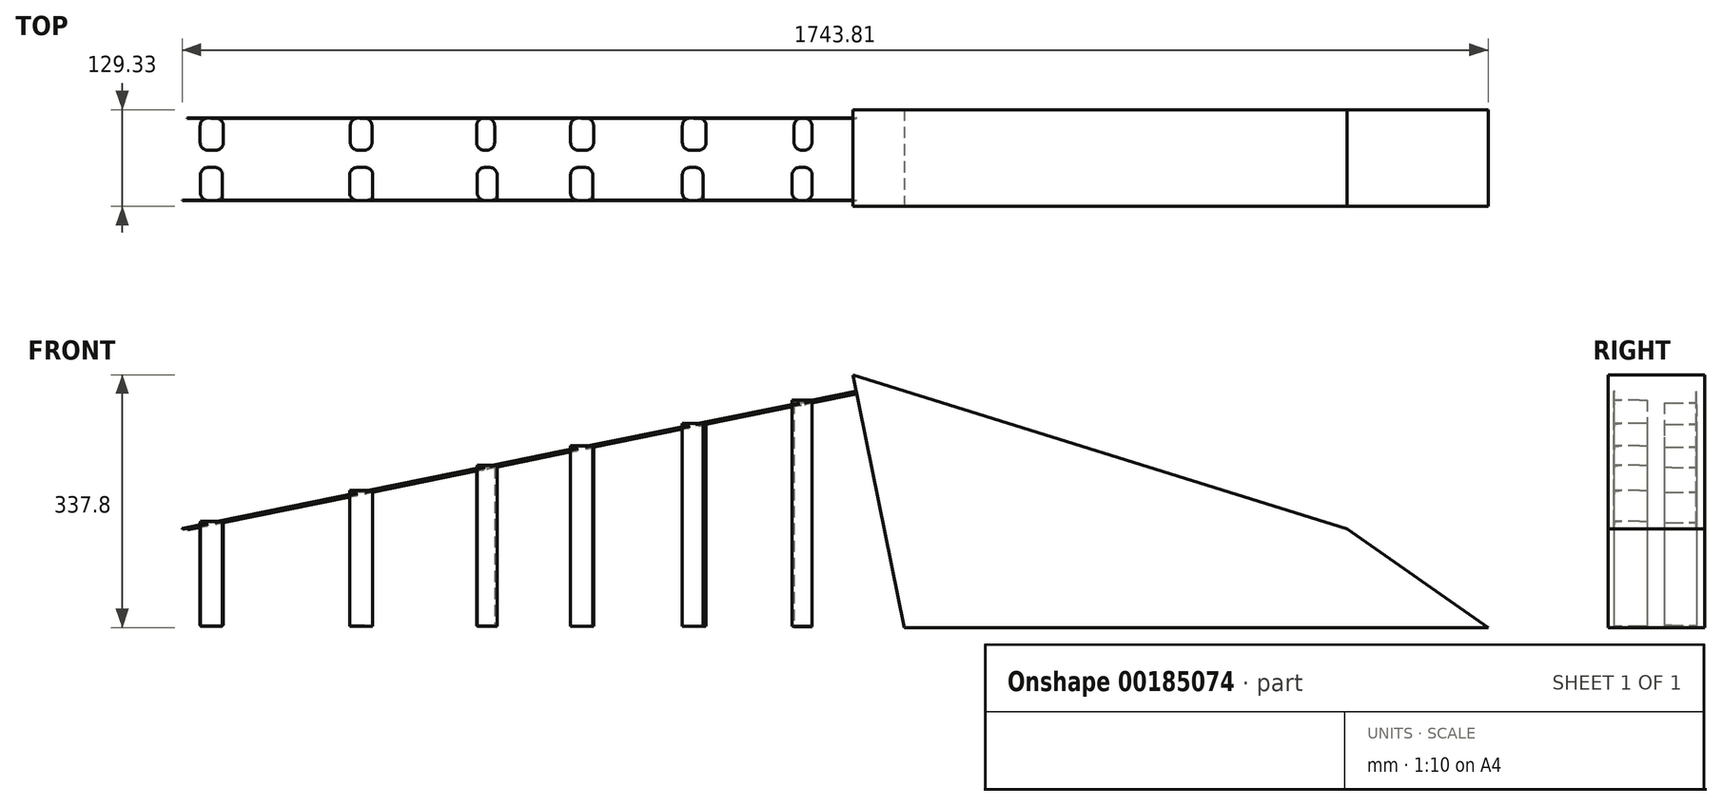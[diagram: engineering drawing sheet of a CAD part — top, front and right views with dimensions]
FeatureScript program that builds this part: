
annotation { "Feature Type Name" : "Feature", "Feature Type Description" : "" }
export const myFeature = defineFeature(function(context is Context, id is Id, definition is map)
    precondition{}
    {
        {
            var Q0;
            Q0=qCreatedBy(makeId("Front.planeOp"),FACE);
            var sketch = newSketch(context, id + "F0", { "sketchPlane" : qUnion([Q0])});
            skLineSegment(sketch, "E0", {"start": v(883.17, -182.99) * mm, "end": v(694.63, -51.4) * mm});
            skLineSegment(sketch, "E1", {"start": v(694.63, -51.4) * mm, "end": v(34.75, 154.8) * mm});
            skLineSegment(sketch, "E2", {"start": v(34.75, 154.8) * mm, "end": v(103.5, -182.99) * mm});
            skLineSegment(sketch, "E3", {"start": v(103.5, -182.99) * mm, "end": v(883.17, -182.99) * mm});
            skSolve(sketch);
        }
        {
            var Q0;
            Q0 = qSketchRegion(id + "F0", true);
            extrude(context, id + "F1", {"entities" : qUnion([Q0]), "oppositeDirection" : true, "depth" : 129.33 * mm});
        }
        {
            var Q0;
            Q0=makeQuery(id+"F1.opExtrude","SWEPT_FACE",FACE,{"disambiguationData":[OSD([sQuery(id+"F0.wireOp",EDGE,"E2")])]});
            var sketch = newSketch(context, id + "F2", { "sketchPlane" : qUnion([Q0])});
            skCircle(sketch, "E4", {"center": v(-33.96, 115.05) * mm, "radius": 26.4 * mm});
            skCircle(sketch, "E5", {"center": v(-91.6, 115.05) * mm, "radius": 26.3 * mm});
            skSolve(sketch);
        }
        {
            var Q0;
            Q0=sQuery(id+"F2.wireOp",EDGE,"E4");
            var Q1;
            Q1=sQuery(id+"F2.wireOp",EDGE,"E5");
            extrude(context, id + "F3", {"bodyType" : ToolBodyType.SURFACE, "surfaceEntities" : qUnion([Q0, Q1]), "depth" : 912.42 * mm});
        }
        {
            var Q0;
            Q0=makeQuery(id+"F1.opExtrude","SWEPT_FACE",FACE,{"disambiguationData":[OSD([sQuery(id+"F0.wireOp",EDGE,"E2")])]});
            var sketch = newSketch(context, id + "F4", { "sketchPlane" : qUnion([Q0])});
            skLineSegment(sketch, "E6.bottom", {"start": v(-8.52, 122.16) * mm, "end": v(-7.92, 122.16) * mm});
            skLineSegment(sketch, "E6.top", {"start": v(-8.52, 120.85) * mm, "end": v(-7.92, 120.85) * mm});
            skLineSegment(sketch, "E6.left", {"start": v(-8.52, 122.16) * mm, "end": v(-8.52, 120.85) * mm});
            skLineSegment(sketch, "E6.right", {"start": v(-7.92, 122.16) * mm, "end": v(-7.92, 120.85) * mm});
            skSolve(sketch);
        }
        {
            var Q0;
            Q0 = qSketchRegion(id + "F4", true);
            extrude(context, id + "F5", {"entities" : qUnion([Q0]), "operationType" : NewBodyOperationType.ADD, "depth" : 918.35 * mm});
        }
        {
            var Q0;
            Q0=makeQuery(id+"F5.opExtrude","SWEPT_FACE",FACE,{"disambiguationData":[OSD([sQuery(id+"F4.wireOp",EDGE,"E6.right")])]});
            var sketch = newSketch(context, id + "F6", { "sketchPlane" : qUnion([Q0])});
            skLineSegment(sketch, "E7.bottom", {"start": v(-19.45, 120.7) * mm, "end": v(-46.2, 120.7) * mm});
            skLineSegment(sketch, "E7.top", {"start": v(-19.45, -181.37) * mm, "end": v(-46.2, -181.37) * mm});
            skLineSegment(sketch, "E7.left", {"start": v(-19.45, 120.7) * mm, "end": v(-19.45, -181.37) * mm});
            skLineSegment(sketch, "E7.right", {"start": v(-46.2, 120.7) * mm, "end": v(-46.2, -181.37) * mm});
            skLineSegment(sketch, "E8.bottom", {"start": v(-165.16, 89.72) * mm, "end": v(-192.75, 89.72) * mm});
            skLineSegment(sketch, "E8.top", {"start": v(-165.16, -181.37) * mm, "end": v(-192.75, -181.37) * mm});
            skLineSegment(sketch, "E8.left", {"start": v(-165.16, 89.72) * mm, "end": v(-165.16, -181.37) * mm});
            skLineSegment(sketch, "E8.right", {"start": v(-192.75, 89.72) * mm, "end": v(-192.75, -181.37) * mm});
            skLineSegment(sketch, "E9.bottom", {"start": v(-312.41, 59.76) * mm, "end": v(-342.06, 59.76) * mm});
            skLineSegment(sketch, "E9.top", {"start": v(-312.41, -181.37) * mm, "end": v(-342.06, -181.37) * mm});
            skLineSegment(sketch, "E9.left", {"start": v(-312.41, 59.76) * mm, "end": v(-312.41, -181.37) * mm});
            skLineSegment(sketch, "E9.right", {"start": v(-342.06, 59.76) * mm, "end": v(-342.06, -181.37) * mm});
            skLineSegment(sketch, "E10.bottom", {"start": v(-440.02, 33.79) * mm, "end": v(-466.59, 33.79) * mm});
            skLineSegment(sketch, "E10.top", {"start": v(-440.02, -181.37) * mm, "end": v(-466.59, -181.37) * mm});
            skLineSegment(sketch, "E10.left", {"start": v(-440.02, 33.79) * mm, "end": v(-440.02, -181.37) * mm});
            skLineSegment(sketch, "E10.right", {"start": v(-466.59, 33.79) * mm, "end": v(-466.59, -181.37) * mm});
            skLineSegment(sketch, "E11.bottom", {"start": v(-606.07, 0) * mm, "end": v(-636.97, 0) * mm});
            skLineSegment(sketch, "E11.top", {"start": v(-606.07, -181.37) * mm, "end": v(-636.97, -181.37) * mm});
            skLineSegment(sketch, "E11.left", {"start": v(-606.07, 0) * mm, "end": v(-606.07, -181.37) * mm});
            skLineSegment(sketch, "E11.right", {"start": v(-636.97, 0) * mm, "end": v(-636.97, -181.37) * mm});
            skLineSegment(sketch, "E12.bottom", {"start": v(-806.8, -40.85) * mm, "end": v(-836.22, -40.85) * mm});
            skLineSegment(sketch, "E12.top", {"start": v(-806.8, -181.37) * mm, "end": v(-836.22, -181.37) * mm});
            skLineSegment(sketch, "E12.left", {"start": v(-806.8, -40.85) * mm, "end": v(-806.8, -181.37) * mm});
            skLineSegment(sketch, "E12.right", {"start": v(-836.22, -40.85) * mm, "end": v(-836.22, -181.37) * mm});
            skSolve(sketch);
        }
        {
            var Q0;
            Q0 = qSketchRegion(id + "F6", true);
            extrude(context, id + "F7", {"entities" : qUnion([Q0]), "operationType" : NewBodyOperationType.ADD, "oppositeDirection" : true, "depth" : 44.1 * mm});
        }
        {
            var Q0;
            Q0=makeQuery(id+"F1.opExtrude","SWEPT_FACE",FACE,{"disambiguationData":[OSD([sQuery(id+"F0.wireOp",EDGE,"E2")])]});
            var sketch = newSketch(context, id + "F8", { "sketchPlane" : qUnion([Q0])});
            skLineSegment(sketch, "E13.bottom", {"start": v(-117.63, 118.72) * mm, "end": v(-118.1, 118.72) * mm});
            skLineSegment(sketch, "E13.top", {"start": v(-117.63, 122) * mm, "end": v(-118.1, 122) * mm});
            skLineSegment(sketch, "E13.left", {"start": v(-117.63, 118.72) * mm, "end": v(-117.63, 122) * mm});
            skLineSegment(sketch, "E13.right", {"start": v(-118.1, 118.72) * mm, "end": v(-118.1, 122) * mm});
            skSolve(sketch);
        }
        {
            var Q0;
            Q0 = qSketchRegion(id + "F8", true);
            extrude(context, id + "F9", {"entities" : qUnion([Q0]), "operationType" : NewBodyOperationType.ADD, "depth" : 911.62 * mm});
        }
        {
            var Q0;
            Q0=makeQuery(id+"F9.opExtrude","SWEPT_FACE",FACE,{"disambiguationData":[OSD([sQuery(id+"F8.wireOp",EDGE,"E13.right")])]});
            var sketch = newSketch(context, id + "F10", { "sketchPlane" : qUnion([Q0])});
            skLineSegment(sketch, "E14.bottom", {"start": v(19.8, 117.13) * mm, "end": v(43.53, 117.13) * mm});
            skLineSegment(sketch, "E14.top", {"start": v(19.8, -182.09) * mm, "end": v(43.53, -182.09) * mm});
            skLineSegment(sketch, "E14.left", {"start": v(19.8, 117.13) * mm, "end": v(19.8, -182.09) * mm});
            skLineSegment(sketch, "E14.right", {"start": v(43.53, 117.13) * mm, "end": v(43.53, -182.09) * mm});
            skLineSegment(sketch, "E15.bottom", {"start": v(161.03, 88.4) * mm, "end": v(192.7, 88.4) * mm});
            skLineSegment(sketch, "E15.top", {"start": v(161.03, -181.24) * mm, "end": v(192.7, -181.24) * mm});
            skLineSegment(sketch, "E15.left", {"start": v(161.03, 88.4) * mm, "end": v(161.03, -181.24) * mm});
            skLineSegment(sketch, "E15.right", {"start": v(192.7, 88.4) * mm, "end": v(192.7, -181.24) * mm});
            skLineSegment(sketch, "E16.bottom", {"start": v(311.32, 57.8) * mm, "end": v(341.87, 57.8) * mm});
            skLineSegment(sketch, "E16.top", {"start": v(311.32, -181.24) * mm, "end": v(341.87, -181.24) * mm});
            skLineSegment(sketch, "E16.left", {"start": v(311.32, 57.8) * mm, "end": v(311.32, -181.24) * mm});
            skLineSegment(sketch, "E16.right", {"start": v(341.87, 57.8) * mm, "end": v(341.87, -181.24) * mm});
            skLineSegment(sketch, "E17.bottom", {"start": v(443.47, 30.92) * mm, "end": v(467.45, 30.92) * mm});
            skLineSegment(sketch, "E17.top", {"start": v(443.47, -180.4) * mm, "end": v(467.45, -180.4) * mm});
            skLineSegment(sketch, "E17.left", {"start": v(443.47, 30.92) * mm, "end": v(443.47, -180.4) * mm});
            skLineSegment(sketch, "E17.right", {"start": v(467.45, 30.92) * mm, "end": v(467.45, -180.4) * mm});
            skLineSegment(sketch, "E18.bottom", {"start": v(607.24, -2.4) * mm, "end": v(636, -2.4) * mm});
            skLineSegment(sketch, "E18.top", {"start": v(607.24, -180.4) * mm, "end": v(636, -180.4) * mm});
            skLineSegment(sketch, "E18.left", {"start": v(607.24, -2.4) * mm, "end": v(607.24, -180.4) * mm});
            skLineSegment(sketch, "E18.right", {"start": v(636, -2.4) * mm, "end": v(636, -180.4) * mm});
            skLineSegment(sketch, "E19.bottom", {"start": v(805.62, -42.78) * mm, "end": v(836.58, -42.78) * mm});
            skLineSegment(sketch, "E19.top", {"start": v(805.62, -180.4) * mm, "end": v(836.58, -180.4) * mm});
            skLineSegment(sketch, "E19.left", {"start": v(805.62, -42.78) * mm, "end": v(805.62, -180.4) * mm});
            skLineSegment(sketch, "E19.right", {"start": v(836.58, -42.78) * mm, "end": v(836.58, -180.4) * mm});
            skSolve(sketch);
        }
        {
            var Q0;
            Q0 = qSketchRegion(id + "F10", true);
            extrude(context, id + "F11", {"entities" : qUnion([Q0]), "operationType" : NewBodyOperationType.ADD, "oppositeDirection" : true, "depth" : 43.03 * mm});
        }
        {
            var Q0;
            Q0=makeQuery(id+"F11.opExtrude","CAP_EDGE",EDGE,{"disambiguationData":[OSD([sQuery(id+"F10.wireOp",EDGE,"E16.left")])],"isStart":false});
            var Q1;
            Q1=makeQuery(id+"F11.opExtrude","CAP_EDGE",EDGE,{"disambiguationData":[OSD([sQuery(id+"F10.wireOp",EDGE,"E18.left")])],"isStart":false});
            var Q2;
            Q2=makeQuery(id+"F7.opExtrude","CAP_EDGE",EDGE,{"disambiguationData":[OSD([sQuery(id+"F6.wireOp",EDGE,"E8.left")])],"isStart":true});
            var Q3;
            Q3=makeQuery(id+"F7.opExtrude","CAP_EDGE",EDGE,{"disambiguationData":[OSD([sQuery(id+"F6.wireOp",EDGE,"E9.left")])],"isStart":false});
            var Q4;
            Q4=makeQuery(id+"F11.opExtrude","CAP_EDGE",EDGE,{"disambiguationData":[OSD([sQuery(id+"F10.wireOp",EDGE,"E16.right")])],"isStart":false});
            var Q5;
            Q5=makeQuery(id+"F7.opExtrude","CAP_EDGE",EDGE,{"disambiguationData":[OSD([sQuery(id+"F6.wireOp",EDGE,"E11.right")])],"isStart":false});
            var Q6;
            Q6=makeQuery(id+"F11.opExtrude","CAP_EDGE",EDGE,{"disambiguationData":[OSD([sQuery(id+"F10.wireOp",EDGE,"E17.right")])],"isStart":false});
            var Q7;
            Q7=makeQuery(id+"F11.opExtrude","CAP_EDGE",EDGE,{"disambiguationData":[OSD([sQuery(id+"F10.wireOp",EDGE,"E19.left")])],"isStart":true});
            var Q8;
            Q8=makeQuery(id+"F7.opExtrude","CAP_EDGE",EDGE,{"disambiguationData":[OSD([sQuery(id+"F6.wireOp",EDGE,"E7.left")])],"isStart":false});
            var Q9;
            Q9=makeQuery(id+"F11.opExtrude","CAP_EDGE",EDGE,{"disambiguationData":[OSD([sQuery(id+"F10.wireOp",EDGE,"E19.left")])],"isStart":false});
            var Q10;
            Q10=makeQuery(id+"F11.opExtrude","CAP_EDGE",EDGE,{"disambiguationData":[OSD([sQuery(id+"F10.wireOp",EDGE,"E16.left")])],"isStart":true});
            var Q11;
            Q11=makeQuery(id+"F11.opExtrude","CAP_EDGE",EDGE,{"disambiguationData":[OSD([sQuery(id+"F10.wireOp",EDGE,"E14.right")])],"isStart":false});
            var Q12;
            Q12=makeQuery(id+"F7.opExtrude","CAP_EDGE",EDGE,{"disambiguationData":[OSD([sQuery(id+"F6.wireOp",EDGE,"E10.left")])],"isStart":true});
            var Q13;
            Q13=makeQuery(id+"F7.opExtrude","CAP_EDGE",EDGE,{"disambiguationData":[OSD([sQuery(id+"F6.wireOp",EDGE,"E11.left")])],"isStart":true});
            var Q14;
            Q14=makeQuery(id+"F11.opExtrude","CAP_EDGE",EDGE,{"disambiguationData":[OSD([sQuery(id+"F10.wireOp",EDGE,"E17.left")])],"isStart":true});
            var Q15;
            Q15=makeQuery(id+"F11.opExtrude","CAP_EDGE",EDGE,{"disambiguationData":[OSD([sQuery(id+"F10.wireOp",EDGE,"E14.left")])],"isStart":false});
            var Q16;
            {var subQ0=sQuery(id+"F6.wireOp",EDGE,"E11.right");Q16=makeQuery(id+"F7.boolean.opBoolean","SPLIT",EDGE,{"disambiguationData":[TD([makeQuery(id+"F5.opExtrude","SWEPT_FACE",FACE,{"disambiguationData":[OSD([sQuery(id+"F4.wireOp",EDGE,"E6.top")])]})])],"derivedFrom":makeQuery(id+"F7.opExtrude","CAP_EDGE",EDGE,{"disambiguationData":[OSD([subQ0])],"isStart":true})});}
            var Q17;
            Q17=makeQuery(id+"F11.opExtrude","CAP_EDGE",EDGE,{"disambiguationData":[OSD([sQuery(id+"F10.wireOp",EDGE,"E15.left")])],"isStart":false});
            var Q18;
            Q18=makeQuery(id+"F7.opExtrude","CAP_EDGE",EDGE,{"disambiguationData":[OSD([sQuery(id+"F6.wireOp",EDGE,"E12.right")])],"isStart":false});
            var Q19;
            {var subQ0=sQuery(id+"F10.wireOp",EDGE,"E19.right");Q19=makeQuery(id+"F11.boolean.opBoolean","SPLIT",EDGE,{"disambiguationData":[TD([makeQuery(id+"F9.opExtrude","SWEPT_FACE",FACE,{"disambiguationData":[OSD([sQuery(id+"F8.wireOp",EDGE,"E13.bottom")])]})])],"derivedFrom":makeQuery(id+"F11.opExtrude","CAP_EDGE",EDGE,{"disambiguationData":[OSD([subQ0])],"isStart":true})});}
            var Q20;
            {var subQ0=sQuery(id+"F6.wireOp",EDGE,"E8.right");Q20=makeQuery(id+"F7.boolean.opBoolean","SPLIT",EDGE,{"disambiguationData":[TD([makeQuery(id+"F5.opExtrude","SWEPT_FACE",FACE,{"disambiguationData":[OSD([sQuery(id+"F4.wireOp",EDGE,"E6.top")])]})])],"derivedFrom":makeQuery(id+"F7.opExtrude","CAP_EDGE",EDGE,{"disambiguationData":[OSD([subQ0])],"isStart":true})});}
            var Q21;
            Q21=makeQuery(id+"F7.opExtrude","CAP_EDGE",EDGE,{"disambiguationData":[OSD([sQuery(id+"F6.wireOp",EDGE,"E12.left")])],"isStart":false});
            var Q22;
            Q22=makeQuery(id+"F7.opExtrude","CAP_EDGE",EDGE,{"disambiguationData":[OSD([sQuery(id+"F6.wireOp",EDGE,"E12.left")])],"isStart":true});
            var Q23;
            {var subQ0=sQuery(id+"F10.wireOp",EDGE,"E18.right");Q23=makeQuery(id+"F11.boolean.opBoolean","SPLIT",EDGE,{"disambiguationData":[TD([makeQuery(id+"F9.opExtrude","SWEPT_FACE",FACE,{"disambiguationData":[OSD([sQuery(id+"F8.wireOp",EDGE,"E13.bottom")])]})])],"derivedFrom":makeQuery(id+"F11.opExtrude","CAP_EDGE",EDGE,{"disambiguationData":[OSD([subQ0])],"isStart":true})});}
            var Q24;
            Q24=makeQuery(id+"F7.opExtrude","CAP_EDGE",EDGE,{"disambiguationData":[OSD([sQuery(id+"F6.wireOp",EDGE,"E10.right")])],"isStart":false});
            var Q25;
            Q25=makeQuery(id+"F7.opExtrude","CAP_EDGE",EDGE,{"disambiguationData":[OSD([sQuery(id+"F6.wireOp",EDGE,"E9.left")])],"isStart":true});
            var Q26;
            Q26=makeQuery(id+"F7.opExtrude","CAP_EDGE",EDGE,{"disambiguationData":[OSD([sQuery(id+"F6.wireOp",EDGE,"E10.left")])],"isStart":false});
            var Q27;
            {var subQ0=sQuery(id+"F10.wireOp",EDGE,"E16.right");Q27=makeQuery(id+"F11.boolean.opBoolean","SPLIT",EDGE,{"disambiguationData":[TD([makeQuery(id+"F9.opExtrude","SWEPT_FACE",FACE,{"disambiguationData":[OSD([sQuery(id+"F8.wireOp",EDGE,"E13.bottom")])]})])],"derivedFrom":makeQuery(id+"F11.opExtrude","CAP_EDGE",EDGE,{"disambiguationData":[OSD([subQ0])],"isStart":true})});}
            var Q28;
            Q28=makeQuery(id+"F7.opExtrude","CAP_EDGE",EDGE,{"disambiguationData":[OSD([sQuery(id+"F6.wireOp",EDGE,"E9.right")])],"isStart":false});
            var Q29;
            {var subQ0=sQuery(id+"F10.wireOp",EDGE,"E17.right");Q29=makeQuery(id+"F11.boolean.opBoolean","SPLIT",EDGE,{"disambiguationData":[TD([makeQuery(id+"F9.opExtrude","SWEPT_FACE",FACE,{"disambiguationData":[OSD([sQuery(id+"F8.wireOp",EDGE,"E13.bottom")])]})])],"derivedFrom":makeQuery(id+"F11.opExtrude","CAP_EDGE",EDGE,{"disambiguationData":[OSD([subQ0])],"isStart":true})});}
            var Q30;
            {var subQ0=sQuery(id+"F6.wireOp",EDGE,"E10.right");Q30=makeQuery(id+"F7.boolean.opBoolean","SPLIT",EDGE,{"disambiguationData":[TD([makeQuery(id+"F5.opExtrude","SWEPT_FACE",FACE,{"disambiguationData":[OSD([sQuery(id+"F4.wireOp",EDGE,"E6.top")])]})])],"derivedFrom":makeQuery(id+"F7.opExtrude","CAP_EDGE",EDGE,{"disambiguationData":[OSD([subQ0])],"isStart":true})});}
            var Q31;
            Q31=makeQuery(id+"F7.opExtrude","CAP_EDGE",EDGE,{"disambiguationData":[OSD([sQuery(id+"F6.wireOp",EDGE,"E7.right")])],"isStart":false});
            var Q32;
            Q32=makeQuery(id+"F7.opExtrude","CAP_EDGE",EDGE,{"disambiguationData":[OSD([sQuery(id+"F6.wireOp",EDGE,"E11.left")])],"isStart":false});
            var Q33;
            Q33=makeQuery(id+"F11.opExtrude","CAP_EDGE",EDGE,{"disambiguationData":[OSD([sQuery(id+"F10.wireOp",EDGE,"E19.right")])],"isStart":false});
            var Q34;
            Q34=makeQuery(id+"F11.opExtrude","CAP_EDGE",EDGE,{"disambiguationData":[OSD([sQuery(id+"F10.wireOp",EDGE,"E18.right")])],"isStart":false});
            var Q35;
            {var subQ0=sQuery(id+"F10.wireOp",EDGE,"E15.right");Q35=makeQuery(id+"F11.boolean.opBoolean","SPLIT",EDGE,{"disambiguationData":[TD([makeQuery(id+"F9.opExtrude","SWEPT_FACE",FACE,{"disambiguationData":[OSD([sQuery(id+"F8.wireOp",EDGE,"E13.bottom")])]})])],"derivedFrom":makeQuery(id+"F11.opExtrude","CAP_EDGE",EDGE,{"disambiguationData":[OSD([subQ0])],"isStart":true})});}
            var Q36;
            Q36=makeQuery(id+"F7.opExtrude","CAP_EDGE",EDGE,{"disambiguationData":[OSD([sQuery(id+"F6.wireOp",EDGE,"E7.left")])],"isStart":true});
            var Q37;
            {var subQ0=sQuery(id+"F6.wireOp",EDGE,"E12.right");Q37=makeQuery(id+"F7.boolean.opBoolean","SPLIT",EDGE,{"disambiguationData":[TD([makeQuery(id+"F5.opExtrude","SWEPT_FACE",FACE,{"disambiguationData":[OSD([sQuery(id+"F4.wireOp",EDGE,"E6.top")])]})])],"derivedFrom":makeQuery(id+"F7.opExtrude","CAP_EDGE",EDGE,{"disambiguationData":[OSD([subQ0])],"isStart":true})});}
            var Q38;
            Q38=makeQuery(id+"F11.opExtrude","CAP_EDGE",EDGE,{"disambiguationData":[OSD([sQuery(id+"F10.wireOp",EDGE,"E15.right")])],"isStart":false});
            var Q39;
            {var subQ1=sQuery(id+"F6.wireOp",EDGE,"E7.right");Q39=makeQuery(id+"F7.boolean.opBoolean","SPLIT",EDGE,{"disambiguationData":[TD([makeQuery(id+"F5.opExtrude","SWEPT_FACE",FACE,{"disambiguationData":[OSD([sQuery(id+"F4.wireOp",EDGE,"E6.top")])]})])],"derivedFrom":makeQuery(id+"F7.opExtrude","CAP_EDGE",EDGE,{"disambiguationData":[OSD([subQ1])],"isStart":true})});}
            var Q40;
            Q40=makeQuery(id+"F7.opExtrude","CAP_EDGE",EDGE,{"disambiguationData":[OSD([sQuery(id+"F6.wireOp",EDGE,"E8.left")])],"isStart":false});
            var Q41;
            Q41=makeQuery(id+"F11.opExtrude","CAP_EDGE",EDGE,{"disambiguationData":[OSD([sQuery(id+"F10.wireOp",EDGE,"E14.left")])],"isStart":true});
            var Q42;
            Q42=makeQuery(id+"F11.opExtrude","CAP_EDGE",EDGE,{"disambiguationData":[OSD([sQuery(id+"F10.wireOp",EDGE,"E17.left")])],"isStart":false});
            var Q43;
            Q43=makeQuery(id+"F7.opExtrude","CAP_EDGE",EDGE,{"disambiguationData":[OSD([sQuery(id+"F6.wireOp",EDGE,"E8.right")])],"isStart":false});
            var Q44;
            Q44=makeQuery(id+"F11.opExtrude","CAP_EDGE",EDGE,{"disambiguationData":[OSD([sQuery(id+"F10.wireOp",EDGE,"E18.left")])],"isStart":true});
            var Q45;
            {var subQ0=sQuery(id+"F6.wireOp",EDGE,"E9.right");Q45=makeQuery(id+"F7.boolean.opBoolean","SPLIT",EDGE,{"disambiguationData":[TD([makeQuery(id+"F5.opExtrude","SWEPT_FACE",FACE,{"disambiguationData":[OSD([sQuery(id+"F4.wireOp",EDGE,"E6.top")])]})])],"derivedFrom":makeQuery(id+"F7.opExtrude","CAP_EDGE",EDGE,{"disambiguationData":[OSD([subQ0])],"isStart":true})});}
            var Q46;
            {var subQ0=sQuery(id+"F10.wireOp",EDGE,"E14.right");Q46=makeQuery(id+"F11.boolean.opBoolean","SPLIT",EDGE,{"disambiguationData":[TD([makeQuery(id+"F9.opExtrude","SWEPT_FACE",FACE,{"disambiguationData":[OSD([sQuery(id+"F8.wireOp",EDGE,"E13.bottom")])]})])],"derivedFrom":makeQuery(id+"F11.opExtrude","CAP_EDGE",EDGE,{"disambiguationData":[OSD([subQ0])],"isStart":true})});}
            var Q47;
            Q47=makeQuery(id+"F11.opExtrude","CAP_EDGE",EDGE,{"disambiguationData":[OSD([sQuery(id+"F10.wireOp",EDGE,"E15.left")])],"isStart":true});
            fillet(context, id + "F12", {"entities" : qUnion([Q0, Q1, Q2, Q3, Q4, Q5, Q6, Q7, Q8, Q9, Q10, Q11, Q12, Q13, Q14, Q15, Q16, Q17, Q18, Q19, Q20, Q21, Q22, Q23, Q24, Q25, Q26, Q27, Q28, Q29, Q30, Q31, Q32, Q33, Q34, Q35, Q36, Q37, Q38, Q39, Q40, Q41, Q42, Q43, Q44, Q45, Q46, Q47]), "radius" : 10.16 * mm, "allowEdgeOverflow" : false});
        }
    });
